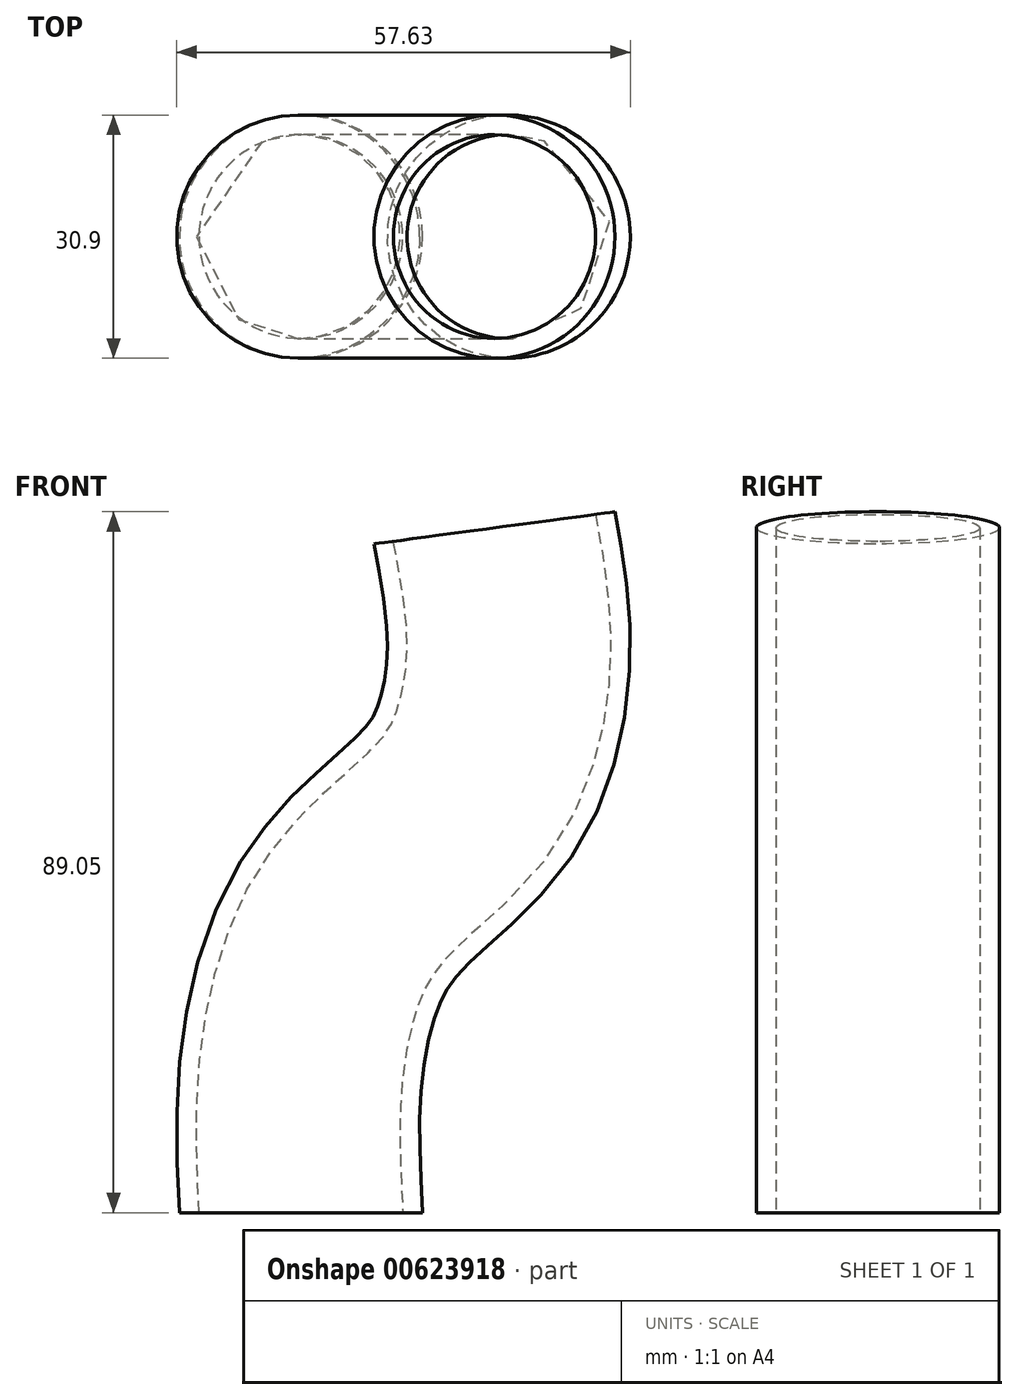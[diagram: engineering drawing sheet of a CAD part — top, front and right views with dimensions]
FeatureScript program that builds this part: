
annotation { "Feature Type Name" : "Feature", "Feature Type Description" : "" }
export const myFeature = defineFeature(function(context is Context, id is Id, definition is map)
    precondition{}
    {
        {
            var Q0;
            Q0=qCreatedBy(makeId("Top.planeOp"),FACE);
            var sketch = newSketch(context, id + "F0", { "sketchPlane" : qUnion([Q0])});
            skCircle(sketch, "E0", {"center": v(0, 0) * mm, "radius": 15.45 * mm});
            skSolve(sketch);
        }
        {
            var Q0;
            Q0=qCreatedBy(makeId("Front.planeOp"),FACE);
            var sketch = newSketch(context, id + "F1", { "sketchPlane" : qUnion([Q0])});
            skFitSpline(sketch, "E1", {"points": [v(0, 0) * mm, v(0, 18.06) * mm, v(4.71, 35.22) * mm, v(13.14, 45.15) * mm, v(22.17, 54.79) * mm, v(26.39, 70.74) * mm, v(24.58, 87) * mm], "startDerivative": vector(-5.14, 100.16) * mm, "endDerivative": vector(-17.56, 94.13) * mm});
            skSolve(sketch);
        }
        {
            var Q0;
            Q0=makeQuery(id+"F0.imprint","IMPRINT",FACE,{"disambiguationData":[TD([[makeQuery(id+"F0.imprint","IMPRINT",EDGE,{"derivedFrom":sQuery(id+"F0.wireOp",EDGE,"E0")}),1.0]])]});
            var Q1;
            Q1=sQuery(id+"F1.wireOp",EDGE,"E1");
            sweep(context, id + "F2", {"profiles" : qUnion([Q0]), "path" : qUnion([Q1])});
        }
        {
            var Q0;
            Q0=makeQuery(id+"F2.opSweep","CAP_FACE",FACE,{"disambiguationData":[OSD([sQuery(id+"F0.wireOp",EDGE,"E0"),sQuery(id+"F1.wireOp",VERTEX,"E1.start")])],"isStart":true});
            var Q1;
            Q1=makeQuery(id+"F2.opSweep","CAP_FACE",FACE,{"disambiguationData":[OSD([sQuery(id+"F0.wireOp",EDGE,"E0"),sQuery(id+"F1.wireOp",VERTEX,"E1.end")])],"isStart":false});
            shell(context, id + "F3", {"entities" : qUnion([Q0, Q1]), "thickness" : 2.5 * mm});
        }
    });
